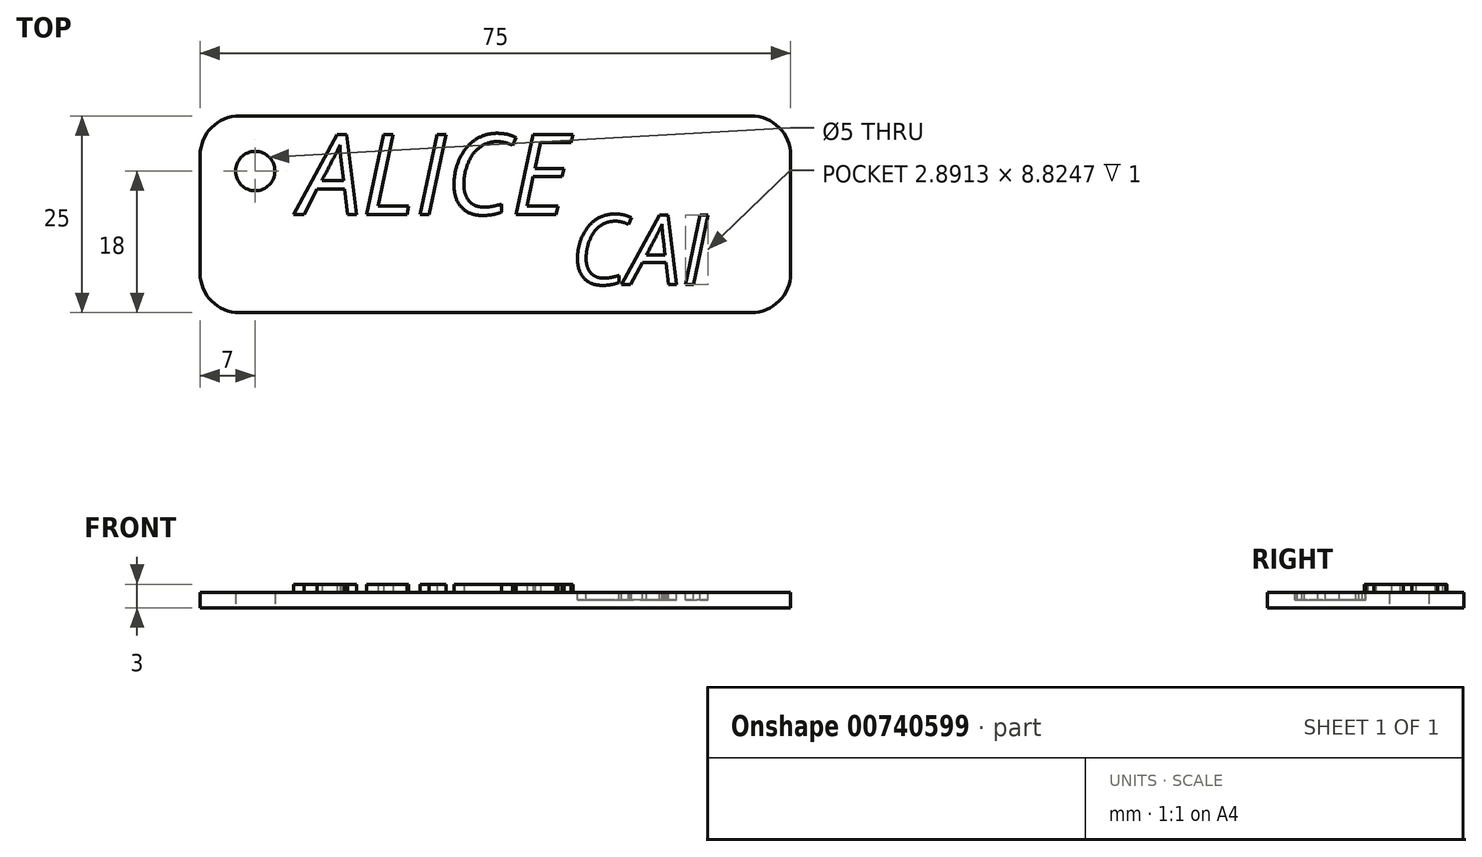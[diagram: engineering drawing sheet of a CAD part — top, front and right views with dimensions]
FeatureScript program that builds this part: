
annotation { "Feature Type Name" : "Feature", "Feature Type Description" : "" }
export const myFeature = defineFeature(function(context is Context, id is Id, definition is map)
    precondition{}
    {
        {
            var Q0;
            Q0=qCreatedBy(makeId("Top.planeOp"),FACE);
            var sketch = newSketch(context, id + "F0", { "sketchPlane" : qUnion([Q0])});
            skLineSegment(sketch, "E0.bottom", {"start": v(-32.5, 12.5) * mm, "end": v(32.5, 12.5) * mm});
            skLineSegment(sketch, "E0.top", {"start": v(-32.5, -12.5) * mm, "end": v(32.5, -12.5) * mm});
            skLineSegment(sketch, "E0.left", {"start": v(-37.5, 7.5) * mm, "end": v(-37.5, -7.5) * mm});
            skLineSegment(sketch, "E0.right", {"start": v(37.5, 7.5) * mm, "end": v(37.5, -7.5) * mm});
            skPoint(sketch, "E0.middle", {"position": v(0, 0) * mm});
            skPoint(sketch, "E1.visualSharp", {"position": v(37.5, 12.5) * mm});
            skArc(sketch, "E1.filletArc", {"start": v(37.5, 7.5) * mm, "mid": v(36.04, 11.04) * mm, "end": v(32.5, 12.5) * mm});
            skPoint(sketch, "E2.visualSharp", {"position": v(37.5, -12.5) * mm});
            skArc(sketch, "E2.filletArc", {"start": v(32.5, -12.5) * mm, "mid": v(36.04, -11.04) * mm, "end": v(37.5, -7.5) * mm});
            skPoint(sketch, "E3.visualSharp", {"position": v(-37.5, -12.5) * mm});
            skArc(sketch, "E3.filletArc", {"start": v(-37.5, -7.5) * mm, "mid": v(-36.04, -11.04) * mm, "end": v(-32.5, -12.5) * mm});
            skPoint(sketch, "E4.visualSharp", {"position": v(-37.5, 12.5) * mm});
            skArc(sketch, "E4.filletArc", {"start": v(-32.5, 12.5) * mm, "mid": v(-36.04, 11.04) * mm, "end": v(-37.5, 7.5) * mm});
            skSolve(sketch);
        }
        {
            var Q0;
            Q0 = qSketchRegion(id + "F0", true);
            extrude(context, id + "F1", {"entities" : qUnion([Q0]), "depth" : 2 * mm, "offsetDistance" : 25 * mm});
        }
        {
            var Q0;
            Q0=qCreatedBy(makeId("Top.planeOp"),FACE);
            var sketch = newSketch(context, id + "F2", { "sketchPlane" : qUnion([Q0])});
            skPoint(sketch, "E5", {"position": v(-30.5, 5.5) * mm});
            skSolve(sketch);
        }
        {
            var Q0;
            Q0=sQuery(id+"F2.wireOp",VERTEX,"E5");
            var Q1;
            Q1=makeQuery(id+"F1.opExtrude","SWEPT_BODY",BODY,{"disambiguationData":[OSD([sQuery(id+"F0.wireOp",EDGE,"E0.bottom"),sQuery(id+"F0.wireOp",EDGE,"E0.top"),sQuery(id+"F0.wireOp",EDGE,"E0.left"),sQuery(id+"F0.wireOp",EDGE,"E0.right"),sQuery(id+"F0.wireOp",EDGE,"E1.filletArc"),sQuery(id+"F0.wireOp",EDGE,"E2.filletArc"),sQuery(id+"F0.wireOp",EDGE,"E3.filletArc"),sQuery(id+"F0.wireOp",EDGE,"E4.filletArc")])]});
            hole(context, id + "F3", {"style" : HoleStyle.SIMPLE, "endStyle" : HoleEndStyle.THROUGH, "oppositeDirection" : true, "holeDiameter" : 5 * mm, "majorDiameter" : 5 * mm, "isTappedThrough" : true, "tappedDepth" : 12 * mm, "tapClearance" : 3, "locations" : qUnion([Q0]), "scope" : qUnion([Q1])});
        }
        {
            var Q0;
            Q0=qCreatedBy(makeId("Top.planeOp"),FACE);
            var sketch = newSketch(context, id + "F4", { "sketchPlane" : qUnion([Q0])});
            skText(sketch, "E6", { "text": "ALICE", "fontName": "OpenSans-Italic.ttf"});
            const initialGuessF4  = {"E6": [-0.02482, 0, 1, 0, 0.01024]};
            skSetInitialGuess(sketch, initialGuessF4);
            skSolve(sketch);
        }
        {
            var Q0;
            Q0 = qSketchRegion(id + "F4", true);
            extrude(context, id + "F5", {"entities" : qUnion([Q0]), "operationType" : NewBodyOperationType.ADD, "depth" : 3 * mm, "offsetDistance" : 25 * mm});
        }
        {
            var Q0;
            {var subQ0=sQuery(id+"F0.wireOp",EDGE,"E0.right");var subQ1=sQuery(id+"F0.wireOp",EDGE,"E0.top");var subQ2=sQuery(id+"F0.wireOp",EDGE,"E0.bottom");var subQ3=sQuery(id+"F0.wireOp",EDGE,"E4.filletArc");var subQ4=sQuery(id+"F0.wireOp",EDGE,"E2.filletArc");var subQ5=sQuery(id+"F0.wireOp",EDGE,"E3.filletArc");var subQ6=sQuery(id+"F0.wireOp",EDGE,"E1.filletArc");var subQ7=sQuery(id+"F0.wireOp",EDGE,"E0.left");Q0=makeQuery(id+"F5.boolean.opBoolean","SPLIT",FACE,{"disambiguationData":[TD([makeQuery(id+"F1.opExtrude","SWEPT_FACE",FACE,{"disambiguationData":[OSD([subQ2])]})])],"derivedFrom":makeQuery(id+"F1.opExtrude","CAP_FACE",FACE,{"disambiguationData":[OSD([subQ2,subQ1,subQ7,subQ0,subQ6,subQ4,subQ5,subQ3])],"isStart":false})});}
            var sketch = newSketch(context, id + "F6", { "sketchPlane" : qUnion([Q0])});
            skText(sketch, "E7", { "text": "CAI", "fontName": "OpenSans-Italic.ttf"});
            const initialGuessF6  = {"E7": [0.00953, -0.0089, 1, 0, 0.0089]};
            skSetInitialGuess(sketch, initialGuessF6);
            skSolve(sketch);
        }
        {
            var Q0;
            Q0 = qSketchRegion(id + "F6", true);
            extrude(context, id + "F7", {"entities" : qUnion([Q0]), "operationType" : NewBodyOperationType.REMOVE, "oppositeDirection" : true, "depth" : 1 * mm, "offsetDistance" : 25 * mm});
        }
    });
